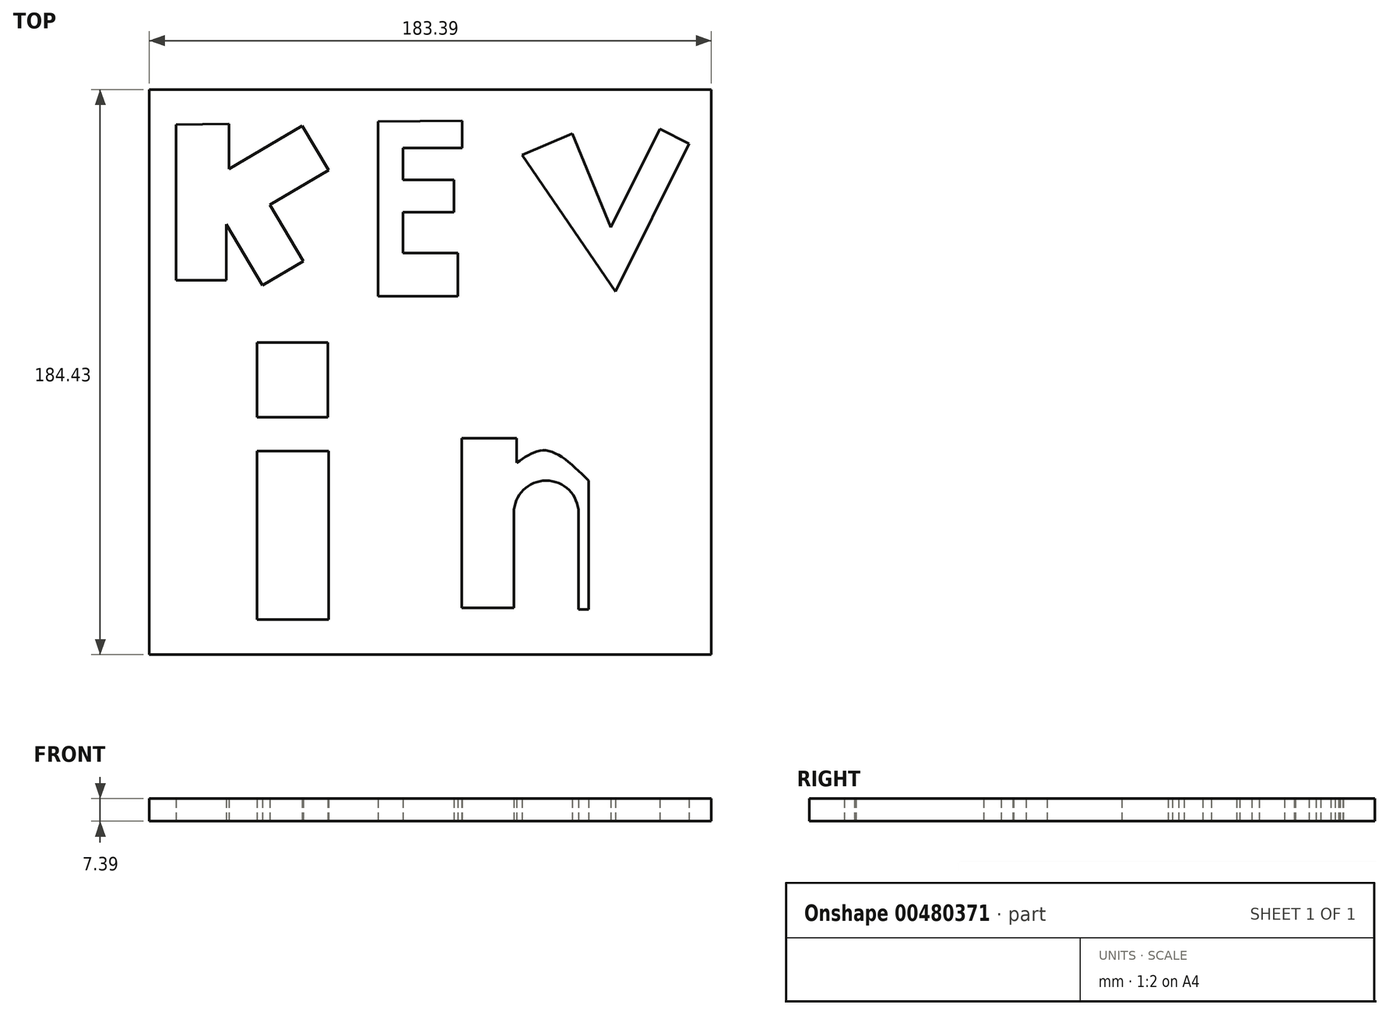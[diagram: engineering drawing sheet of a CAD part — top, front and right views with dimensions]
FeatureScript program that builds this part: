
annotation { "Feature Type Name" : "Feature", "Feature Type Description" : "" }
export const myFeature = defineFeature(function(context is Context, id is Id, definition is map)
    precondition{}
    {
        {
            var Q0;
            Q0=qCreatedBy(makeId("Top.planeOp"),FACE);
            var sketch = newSketch(context, id + "F0", { "sketchPlane" : qUnion([Q0])});
            skLineSegment(sketch, "E0.bottom", {"start": v(-91.49, 91.49) * mm, "end": v(91.9, 91.49) * mm});
            skLineSegment(sketch, "E0.top", {"start": v(-91.49, -92.94) * mm, "end": v(91.9, -92.94) * mm});
            skLineSegment(sketch, "E0.left", {"start": v(-91.49, 91.49) * mm, "end": v(-91.49, -92.94) * mm});
            skLineSegment(sketch, "E0.right", {"start": v(91.9, 91.49) * mm, "end": v(91.9, -92.94) * mm});
            skLineSegment(sketch, "E1", {"start": v(-82.78, 80.08) * mm, "end": v(-82.78, 29.25) * mm});
            skLineSegment(sketch, "E2", {"start": v(-82.78, 29.25) * mm, "end": v(-66.39, 29.25) * mm});
            skLineSegment(sketch, "E3", {"start": v(-66.39, 29.25) * mm, "end": v(-66.39, 47.5) * mm});
            skLineSegment(sketch, "E4", {"start": v(-66.39, 47.5) * mm, "end": v(-54.56, 27.6) * mm});
            skLineSegment(sketch, "E5", {"start": v(-54.56, 27.6) * mm, "end": v(-41.3, 35.46) * mm});
            skLineSegment(sketch, "E6", {"start": v(-41.3, 35.46) * mm, "end": v(-52.2, 53.83) * mm});
            skLineSegment(sketch, "E7", {"start": v(-52.2, 53.83) * mm, "end": v(-33.04, 65.2) * mm});
            skLineSegment(sketch, "E8", {"start": v(-33.04, 65.2) * mm, "end": v(-41.66, 79.72) * mm});
            skLineSegment(sketch, "E9", {"start": v(-41.66, 79.72) * mm, "end": v(-65.47, 65.58) * mm});
            skLineSegment(sketch, "E10", {"start": v(-65.47, 65.58) * mm, "end": v(-65.47, 80.29) * mm});
            skLineSegment(sketch, "E11", {"start": v(-65.47, 80.29) * mm, "end": v(-82.78, 80.08) * mm});
            skLineSegment(sketch, "E12", {"start": v(-16.8, 81.12) * mm, "end": v(-16.8, 24.07) * mm});
            skLineSegment(sketch, "E13", {"start": v(-16.8, 24.07) * mm, "end": v(9.13, 24.07) * mm});
            skLineSegment(sketch, "E14", {"start": v(9.13, 24.07) * mm, "end": v(9.13, 38.17) * mm});
            skLineSegment(sketch, "E15", {"start": v(9.13, 38.17) * mm, "end": v(-8.71, 38.17) * mm});
            skLineSegment(sketch, "E16", {"start": v(-8.71, 38.17) * mm, "end": v(-8.71, 51.45) * mm});
            skLineSegment(sketch, "E17", {"start": v(-8.71, 51.45) * mm, "end": v(7.88, 51.45) * mm});
            skLineSegment(sketch, "E18", {"start": v(7.88, 51.45) * mm, "end": v(7.88, 62.03) * mm});
            skLineSegment(sketch, "E19", {"start": v(7.88, 62.03) * mm, "end": v(-8.71, 62.03) * mm});
            skLineSegment(sketch, "E20", {"start": v(-8.71, 62.03) * mm, "end": v(-8.71, 72.4) * mm});
            skLineSegment(sketch, "E21", {"start": v(-8.71, 72.4) * mm, "end": v(10.58, 72.4) * mm});
            skLineSegment(sketch, "E22", {"start": v(10.58, 72.4) * mm, "end": v(10.58, 81.32) * mm});
            skLineSegment(sketch, "E23", {"start": v(10.58, 81.32) * mm, "end": v(-16.8, 81.12) * mm});
            skLineSegment(sketch, "E24", {"start": v(46.47, 77.17) * mm, "end": v(30.08, 70.12) * mm});
            skLineSegment(sketch, "E25", {"start": v(30.08, 70.12) * mm, "end": v(60.58, 25.52) * mm});
            skLineSegment(sketch, "E26", {"start": v(60.58, 25.52) * mm, "end": v(84.64, 73.85) * mm});
            skLineSegment(sketch, "E27", {"start": v(84.64, 73.85) * mm, "end": v(75.09, 78.61) * mm});
            skLineSegment(sketch, "E28", {"start": v(75.09, 78.61) * mm, "end": v(59.1, 46.48) * mm});
            skLineSegment(sketch, "E29", {"start": v(59.1, 46.48) * mm, "end": v(46.47, 77.17) * mm});
            skLineSegment(sketch, "E30.bottom", {"start": v(-56.42, 8.99) * mm, "end": v(-33.2, 8.99) * mm});
            skLineSegment(sketch, "E30.top", {"start": v(-56.42, -15.42) * mm, "end": v(-33.2, -15.42) * mm});
            skLineSegment(sketch, "E30.left", {"start": v(-56.42, 8.99) * mm, "end": v(-56.42, -15.42) * mm});
            skLineSegment(sketch, "E30.right", {"start": v(-33.2, 8.99) * mm, "end": v(-33.2, -15.42) * mm});
            skLineSegment(sketch, "E31.bottom", {"start": v(-56.42, -26.55) * mm, "end": v(-32.96, -26.55) * mm});
            skLineSegment(sketch, "E31.top", {"start": v(-56.42, -81.52) * mm, "end": v(-32.96, -81.52) * mm});
            skLineSegment(sketch, "E31.left", {"start": v(-56.42, -26.55) * mm, "end": v(-56.42, -81.52) * mm});
            skLineSegment(sketch, "E31.right", {"start": v(-32.96, -26.55) * mm, "end": v(-32.96, -81.52) * mm});
            skLineSegment(sketch, "E32", {"start": v(10.4, -22.29) * mm, "end": v(10.4, -77.72) * mm});
            skLineSegment(sketch, "E33", {"start": v(10.4, -77.72) * mm, "end": v(27.45, -77.72) * mm});
            skLineSegment(sketch, "E34", {"start": v(27.45, -77.72) * mm, "end": v(27.45, -46.69) * mm});
            skArc(sketch, "E35", {"start": v(27.45, -46.69) * mm, "mid": v(38, -36.15) * mm, "end": v(48.54, -46.69) * mm});
            skLineSegment(sketch, "E36", {"start": v(48.54, -46.69) * mm, "end": v(48.54, -78.2) * mm});
            skLineSegment(sketch, "E37", {"start": v(48.54, -78.2) * mm, "end": v(66.54, -78.2) * mm});
            skLineSegment(sketch, "E38", {"start": v(66.54, -78.2) * mm, "end": v(66.54, -39.82) * mm});
            skPoint(sketch, "E39.end.orphan", {"position": v(67.5, -22.29) * mm});
            skPoint(sketch, "E40.start.orphan", {"position": v(20.82, -22.29) * mm});
            skLineSegment(sketch, "E41", {"start": v(10.4, -22.29) * mm, "end": v(20.82, -22.29) * mm});
            skLineSegment(sketch, "E42", {"start": v(20.82, -22.29) * mm, "end": v(28.4, -22.29) * mm});
            skLineSegment(sketch, "E43", {"start": v(28.4, -30.34) * mm, "end": v(28.4, -22.29) * mm});
            skPoint(sketch, "E44.1.internal.snap0", {"position": v(38, -36.15) * mm});
            skPoint(sketch, "E44.1.internal.snap1", {"position": v(28.4, -26.31) * mm});
            skPoint(sketch, "E44.2.internal.snap0", {"position": v(38, -36.15) * mm});
            skFitSpline(sketch, "E44", {"points": [v(28.4, -30.34) * mm, v(38, -26.31) * mm, v(51.86, -36.15) * mm], "startDerivative": vector(21.23, 15.04) * mm, "endDerivative": vector(25.5, -25.02) * mm});
            skLineSegment(sketch, "E45", {"start": v(51.86, -36.15) * mm, "end": v(48.54, -78.2) * mm});
            skLineSegment(sketch, "E46", {"start": v(51.86, -36.15) * mm, "end": v(51.86, -102.6) * mm});
            skSolve(sketch);
        }
        {
            var Q0;
            Q0=makeQuery(id+"F0.imprint","IMPRINT",FACE,{"disambiguationData":[TD([[makeQuery(id+"F0.imprint","IMPRINT",EDGE,{"derivedFrom":sQuery(id+"F0.wireOp",EDGE,"E0.bottom")}),-1.0]])]});
            extrude(context, id + "F1", {"entities" : qUnion([Q0]), "depth" : 7.4 * mm});
        }
    });
